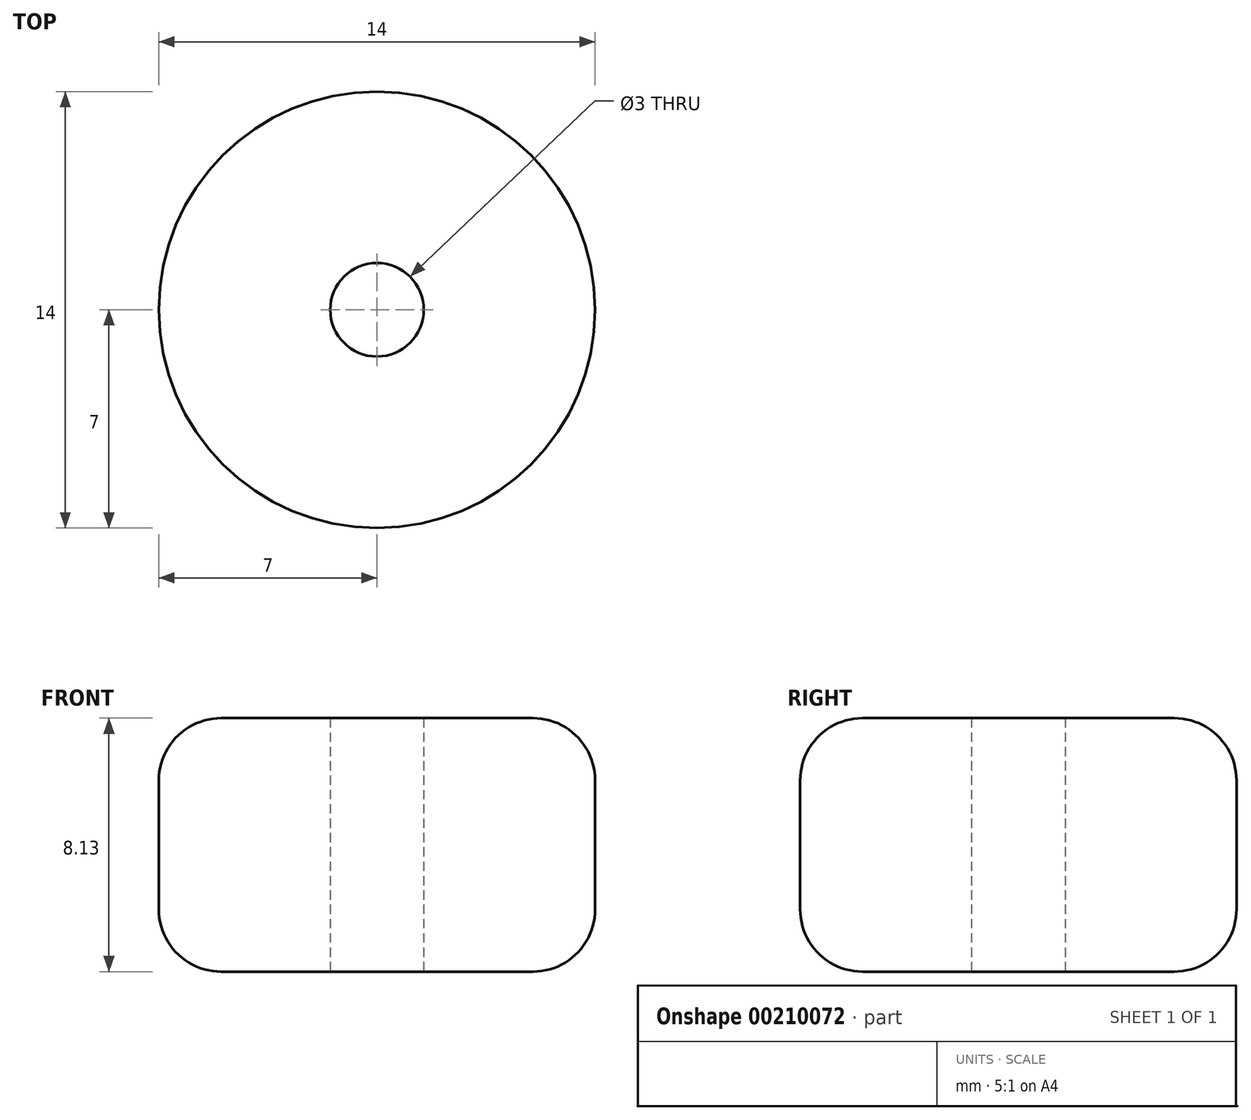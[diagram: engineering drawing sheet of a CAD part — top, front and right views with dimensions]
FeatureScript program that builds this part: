
annotation { "Feature Type Name" : "Feature", "Feature Type Description" : "" }
export const myFeature = defineFeature(function(context is Context, id is Id, definition is map)
    precondition{}
    {
        {
            var Q0;
            Q0=qCreatedBy(makeId("Top.planeOp"),FACE);
            var sketch = newSketch(context, id + "F0", { "sketchPlane" : qUnion([Q0])});
            skCircle(sketch, "E0", {"center": v(0, 0) * mm, "radius": 7 * mm});
            skCircle(sketch, "E1", {"center": v(0, 0) * mm, "radius": 1.5 * mm});
            skSolve(sketch);
        }
        {
            var Q0;
            Q0=makeQuery(id+"F0.imprint","IMPRINT",FACE,{"disambiguationData":[TD([[makeQuery(id+"F0.imprint","IMPRINT",EDGE,{"derivedFrom":sQuery(id+"F0.wireOp",EDGE,"E0")}),1.0]])]});
            extrude(context, id + "F1", {"entities" : qUnion([Q0]), "depth" : 8.13 * mm});
        }
        {
            var Q0;
            Q0=makeQuery(id+"F1.opExtrude","CAP_EDGE",EDGE,{"disambiguationData":[OSD([sQuery(id+"F0.wireOp",EDGE,"E0")])],"isStart":false});
            fillet(context, id + "F2", {"entities" : qUnion([Q0]), "radius" : 2 * mm, "tangentPropagation" : true, "allowEdgeOverflow" : false});
        }
        {
            var Q0;
            Q0=makeQuery(id+"F1.opExtrude","CAP_EDGE",EDGE,{"disambiguationData":[OSD([sQuery(id+"F0.wireOp",EDGE,"E0")])],"isStart":true});
            fillet(context, id + "F3", {"entities" : qUnion([Q0]), "radius" : 2 * mm, "tangentPropagation" : true, "allowEdgeOverflow" : false});
        }
    });
